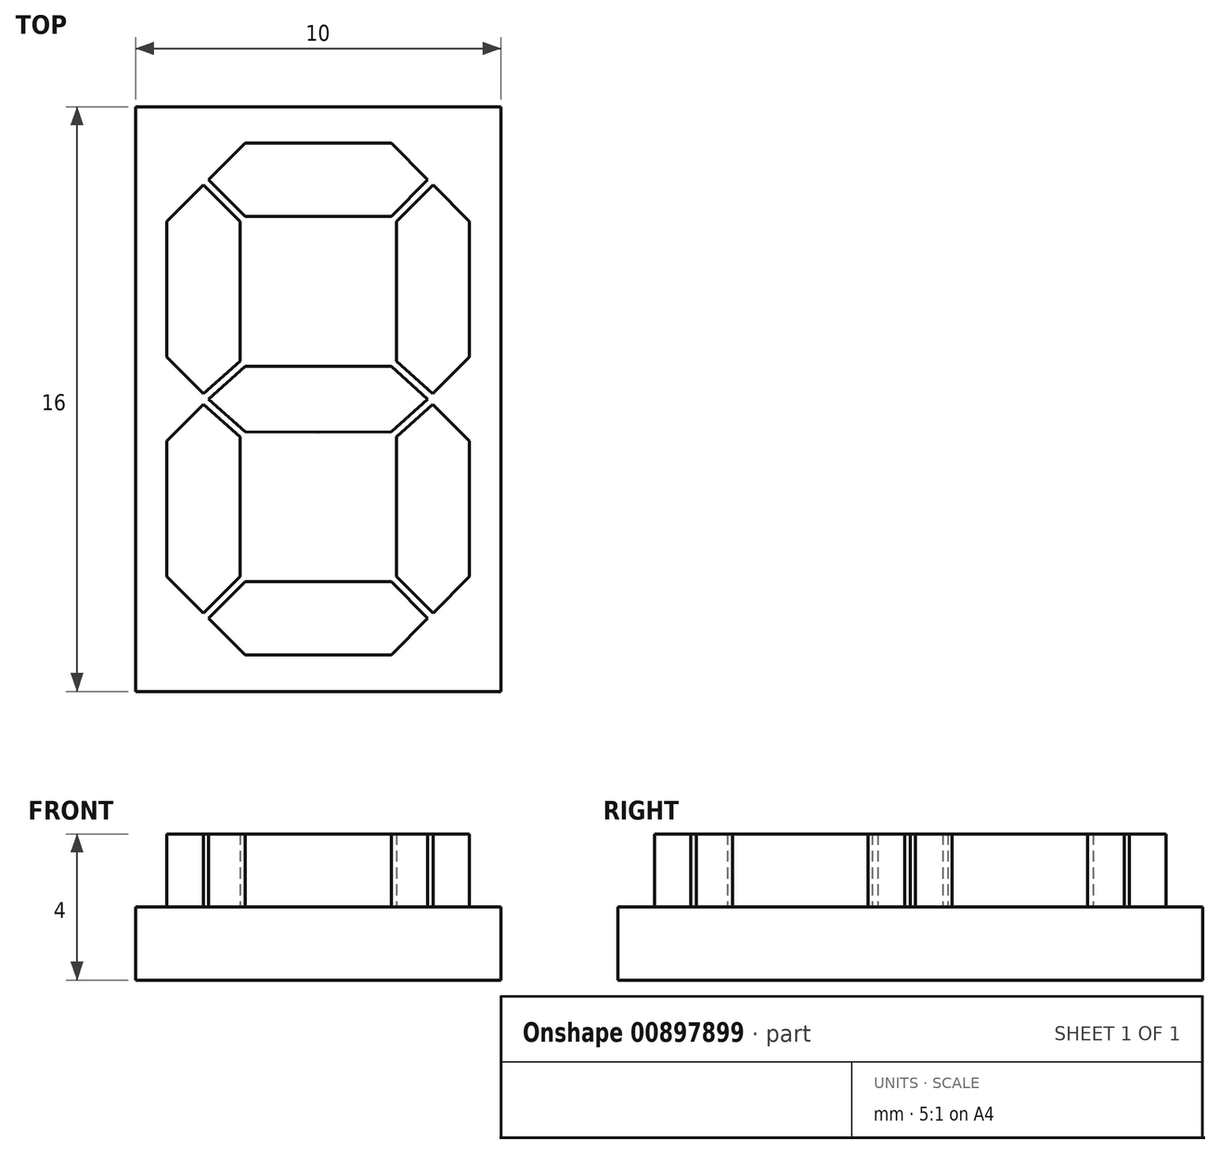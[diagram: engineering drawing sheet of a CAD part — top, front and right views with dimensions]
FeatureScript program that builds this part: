
annotation { "Feature Type Name" : "Feature", "Feature Type Description" : "" }
export const myFeature = defineFeature(function(context is Context, id is Id, definition is map)
    precondition{}
    {
        {
            var Q0;
            Q0=qCreatedBy(makeId("Top.planeOp"),FACE);
            var sketch = newSketch(context, id + "F0", { "sketchPlane" : qUnion([Q0])});
            skLineSegment(sketch, "E0.bottom", {"start": v(5, -8) * mm, "end": v(-5, -8) * mm});
            skLineSegment(sketch, "E0.top", {"start": v(5, 8) * mm, "end": v(-5, 8) * mm});
            skLineSegment(sketch, "E0.left", {"start": v(5, -8) * mm, "end": v(5, 8) * mm});
            skLineSegment(sketch, "E0.right", {"start": v(-5, -8) * mm, "end": v(-5, 8) * mm});
            skPoint(sketch, "E0.middle", {"position": v(0, 0) * mm});
            skSolve(sketch);
        }
        {
            var Q0;
            Q0=makeQuery(id+"F0.imprint","IMPRINT",FACE,{"disambiguationData":[TD([[makeQuery(id+"F0.imprint","IMPRINT",EDGE,{"derivedFrom":sQuery(id+"F0.wireOp",EDGE,"E0.bottom")}),-1.0]])]});
            extrude(context, id + "F1", {"entities" : qUnion([Q0]), "depth" : 2 * mm, "offsetDistance" : 25 * mm});
        }
        {
            var Q0;
            Q0=makeQuery(id+"F1.opExtrude","CAP_FACE",FACE,{"disambiguationData":[OSD([sQuery(id+"F0.wireOp",EDGE,"E0.bottom"),sQuery(id+"F0.wireOp",EDGE,"E0.top"),sQuery(id+"F0.wireOp",EDGE,"E0.left"),sQuery(id+"F0.wireOp",EDGE,"E0.right")])],"isStart":false});
            var sketch = newSketch(context, id + "F2", { "sketchPlane" : qUnion([Q0])});
            skLineSegment(sketch, "E1", {"start": v(-3, 8) * mm, "end": v(-3, -8) * mm, "construction": true});
            skLineSegment(sketch, "E2.0.1.0", {"start": v(-5, 6) * mm, "end": v(5, 6) * mm, "construction": true});
            skLineSegment(sketch, "E2.direction2", {"start": v(-5, 7) * mm, "end": v(-5, 6) * mm, "construction": true});
            skLineSegment(sketch, "E3.1.0.0", {"start": v(-2, 8) * mm, "end": v(-2, -8) * mm, "construction": true});
            skLineSegment(sketch, "E3.3.0.0", {"start": v(0, 8) * mm, "end": v(0, -8) * mm, "construction": true});
            skLineSegment(sketch, "E3.direction1", {"start": v(-3, -8) * mm, "end": v(-2, -8) * mm, "construction": true});
            skLineSegment(sketch, "E4", {"start": v(-2, 7) * mm, "end": v(-3, 6) * mm});
            skLineSegment(sketch, "E5", {"start": v(-3, 6) * mm, "end": v(-2, 5) * mm});
            skLineSegment(sketch, "E6", {"start": v(-2, 5) * mm, "end": v(0, 5) * mm});
            skLineSegment(sketch, "E7", {"start": v(-2, 7) * mm, "end": v(0, 7) * mm});
            skLineSegment(sketch, "E8.0", {"start": v(-3.14, 5.86) * mm, "end": v(-2.14, 4.86) * mm});
            skLineSegment(sketch, "E9", {"start": v(-2.14, 4.86) * mm, "end": v(-2.14, 1.03) * mm});
            skLineSegment(sketch, "E10.0", {"start": v(-4.14, 4.86) * mm, "end": v(-4.14, 1.15) * mm});
            skLineSegment(sketch, "E11", {"start": v(-3.14, 5.86) * mm, "end": v(-4.14, 4.86) * mm});
            skLineSegment(sketch, "E12", {"start": v(-4.14, 4.86) * mm, "end": v(5, 4.86) * mm, "construction": true});
            skLineSegment(sketch, "E13", {"start": v(0, 0.9) * mm, "end": v(-2, 0.9) * mm});
            skLineSegment(sketch, "E14", {"start": v(-2, 0.9) * mm, "end": v(-3, 0) * mm});
            skLineSegment(sketch, "E15.0", {"start": v(-2.14, 1.03) * mm, "end": v(-3.14, 0.15) * mm});
            skLineSegment(sketch, "E16", {"start": v(-3.14, 5.86) * mm, "end": v(-3.14, 0.15) * mm, "construction": true});
            skLineSegment(sketch, "E17", {"start": v(-4.14, 1.15) * mm, "end": v(-3.14, 0.15) * mm});
            skLineSegment(sketch, "E18.MirrorCS", {"start": v(0, -0.9) * mm, "end": v(-2, -0.9) * mm});
            skLineSegment(sketch, "E19.MirrorCS", {"start": v(-2, -0.9) * mm, "end": v(-3, 0) * mm});
            skLineSegment(sketch, "E20.MirrorCS", {"start": v(-2, -5) * mm, "end": v(0, -5) * mm});
            skLineSegment(sketch, "E21.MirrorCS", {"start": v(-3, -6) * mm, "end": v(-2, -5) * mm});
            skLineSegment(sketch, "E22.MirrorCS", {"start": v(-2, -7) * mm, "end": v(-3, -6) * mm});
            skLineSegment(sketch, "E23.MirrorCS", {"start": v(-2, -7) * mm, "end": v(0, -7) * mm});
            skLineSegment(sketch, "E24.MirrorCS", {"start": v(-3.14, -5.86) * mm, "end": v(-2.14, -4.86) * mm});
            skLineSegment(sketch, "E25.MirrorCS", {"start": v(-3.14, -5.86) * mm, "end": v(-4.14, -4.86) * mm});
            skLineSegment(sketch, "E26.MirrorCS", {"start": v(-4.14, -4.86) * mm, "end": v(-4.14, -1.15) * mm});
            skLineSegment(sketch, "E27.MirrorCS", {"start": v(-4.14, -1.15) * mm, "end": v(-3.14, -0.15) * mm});
            skLineSegment(sketch, "E28.MirrorCS", {"start": v(-2.14, -4.86) * mm, "end": v(-2.14, -1.03) * mm});
            skLineSegment(sketch, "E29.MirrorCS", {"start": v(-2.14, -1.03) * mm, "end": v(-3.14, -0.15) * mm});
            skLineSegment(sketch, "E30.MirrorCS", {"start": v(2, 7) * mm, "end": v(0, 7) * mm});
            skLineSegment(sketch, "E31.MirrorCS", {"start": v(2, 7) * mm, "end": v(3, 6) * mm});
            skLineSegment(sketch, "E32.MirrorCS", {"start": v(3, 6) * mm, "end": v(2, 5) * mm});
            skLineSegment(sketch, "E33.MirrorCS", {"start": v(2, 5) * mm, "end": v(0, 5) * mm});
            skLineSegment(sketch, "E34.MirrorCS", {"start": v(3.14, 5.86) * mm, "end": v(2.14, 4.86) * mm});
            skLineSegment(sketch, "E35.MirrorCS", {"start": v(3.14, 5.86) * mm, "end": v(4.14, 4.86) * mm});
            skLineSegment(sketch, "E36.MirrorCS", {"start": v(4.14, 4.86) * mm, "end": v(4.14, 1.15) * mm});
            skLineSegment(sketch, "E37.MirrorCS", {"start": v(4.14, 1.15) * mm, "end": v(3.14, 0.15) * mm});
            skLineSegment(sketch, "E38.MirrorCS", {"start": v(2.14, 4.86) * mm, "end": v(2.14, 1.03) * mm});
            skLineSegment(sketch, "E39.MirrorCS", {"start": v(2.14, 1.03) * mm, "end": v(3.14, 0.15) * mm});
            skLineSegment(sketch, "E40.MirrorCS", {"start": v(2, 0.9) * mm, "end": v(3, 0) * mm});
            skLineSegment(sketch, "E41.MirrorCS", {"start": v(0, 0.9) * mm, "end": v(2, 0.9) * mm});
            skLineSegment(sketch, "E42.MirrorCS", {"start": v(2, -0.9) * mm, "end": v(3, 0) * mm});
            skLineSegment(sketch, "E43.MirrorCS", {"start": v(0, -0.9) * mm, "end": v(2, -0.9) * mm});
            skLineSegment(sketch, "E44.MirrorCS", {"start": v(2.14, -1.03) * mm, "end": v(3.14, -0.15) * mm});
            skLineSegment(sketch, "E45.MirrorCS", {"start": v(4.14, -1.15) * mm, "end": v(3.14, -0.15) * mm});
            skLineSegment(sketch, "E46.MirrorCS", {"start": v(4.14, -4.86) * mm, "end": v(4.14, -1.15) * mm});
            skLineSegment(sketch, "E47.MirrorCS", {"start": v(2.14, -4.86) * mm, "end": v(2.14, -1.03) * mm});
            skLineSegment(sketch, "E48.MirrorCS", {"start": v(3.14, -5.86) * mm, "end": v(2.14, -4.86) * mm});
            skLineSegment(sketch, "E49.MirrorCS", {"start": v(3.14, -5.86) * mm, "end": v(4.14, -4.86) * mm});
            skLineSegment(sketch, "E50.MirrorCS", {"start": v(3, -6) * mm, "end": v(2, -5) * mm});
            skLineSegment(sketch, "E51.MirrorCS", {"start": v(2, -5) * mm, "end": v(0, -5) * mm});
            skLineSegment(sketch, "E52.MirrorCS", {"start": v(2, -7) * mm, "end": v(3, -6) * mm});
            skLineSegment(sketch, "E53.MirrorCS", {"start": v(2, -7) * mm, "end": v(0, -7) * mm});
            skSolve(sketch);
        }
        {
            var Q0;
            Q0=qSketchRegion(id+"F2",true);
            extrude(context, id + "F3", {"entities" : qUnion([Q0]), "operationType" : NewBodyOperationType.ADD, "depth" : 2 * mm, "offsetDistance" : 25 * mm});
        }
    });
